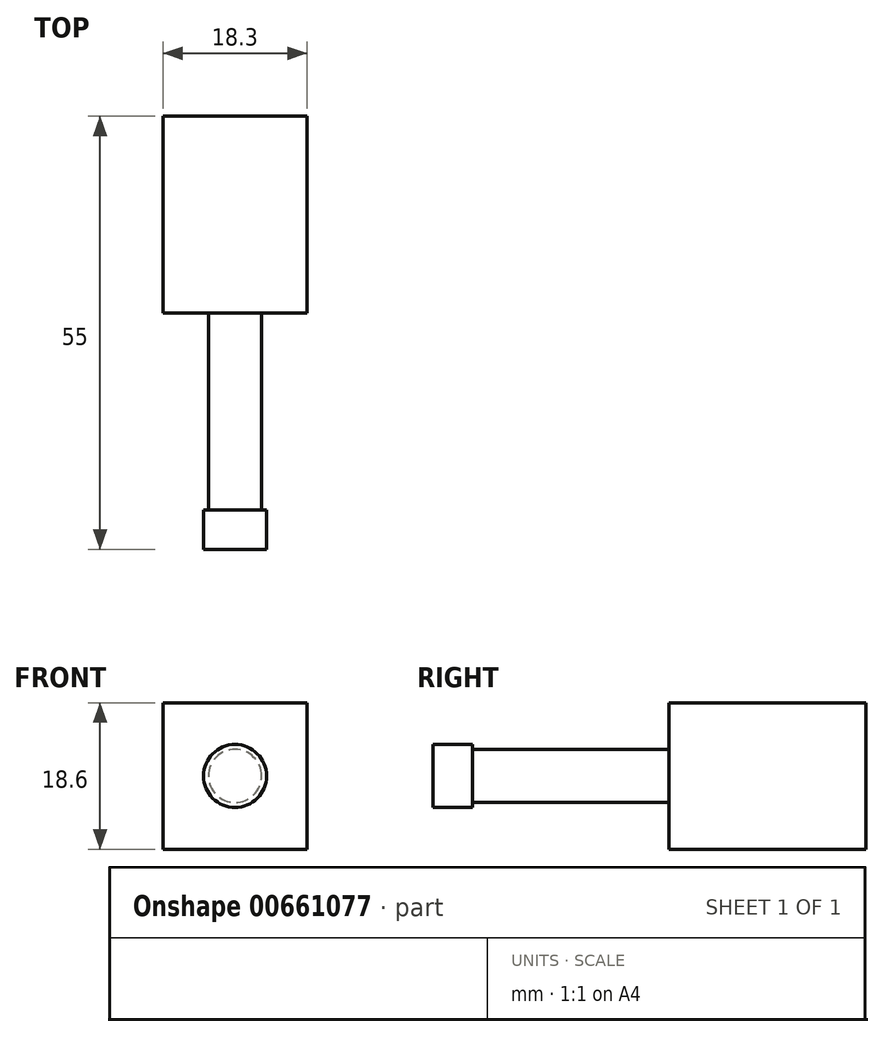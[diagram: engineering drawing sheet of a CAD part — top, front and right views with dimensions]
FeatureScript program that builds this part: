
annotation { "Feature Type Name" : "Feature", "Feature Type Description" : "" }
export const myFeature = defineFeature(function(context is Context, id is Id, definition is map)
    precondition{}
    {
        {
            var Q0;
            Q0=qCreatedBy(makeId("Front.planeOp"),FACE);
            var sketch = newSketch(context, id + "F0", { "sketchPlane" : qUnion([Q0])});
            skCircle(sketch, "E0", {"center": v(0, 0) * mm, "radius": 4 * mm});
            skSolve(sketch);
        }
        {
            var Q0;
            Q0 = qSketchRegion(id + "F0", true);
            extrude(context, id + "F1", {"entities" : qUnion([Q0]), "depth" : 5 * mm, "offsetDistance" : 25 * mm});
        }
        {
            var Q0;
            Q0=qCreatedBy(makeId("Front.planeOp"),FACE);
            var sketch = newSketch(context, id + "F2", { "sketchPlane" : qUnion([Q0])});
            skCircle(sketch, "E1", {"center": v(0, 0) * mm, "radius": 3.37 * mm});
            skSolve(sketch);
        }
        {
            var Q0;
            Q0 = qSketchRegion(id + "F2", true);
            extrude(context, id + "F3", {"entities" : qUnion([Q0]), "operationType" : NewBodyOperationType.ADD, "oppositeDirection" : true, "depth" : 25 * mm, "offsetDistance" : 25 * mm});
        }
        {
            var Q0;
            Q0=makeQuery(id+"F3.opExtrude","CAP_FACE",FACE,{"disambiguationData":[OSD([sQuery(id+"F2.wireOp",EDGE,"E1")])],"isStart":false});
            var sketch = newSketch(context, id + "F4", { "sketchPlane" : qUnion([Q0])});
            skLineSegment(sketch, "E2.bottom", {"start": v(9.15, -9.3) * mm, "end": v(-9.15, -9.3) * mm});
            skLineSegment(sketch, "E2.top", {"start": v(9.15, 9.3) * mm, "end": v(-9.15, 9.3) * mm});
            skLineSegment(sketch, "E2.left", {"start": v(9.15, -9.3) * mm, "end": v(9.15, 9.3) * mm});
            skLineSegment(sketch, "E2.right", {"start": v(-9.15, -9.3) * mm, "end": v(-9.15, 9.3) * mm});
            skPoint(sketch, "E2.middle", {"position": v(0, 0) * mm});
            skSolve(sketch);
        }
        {
            var Q0;
            Q0 = qSketchRegion(id + "F4", true);
            extrude(context, id + "F5", {"entities" : qUnion([Q0]), "operationType" : NewBodyOperationType.ADD, "depth" : 25 * mm, "offsetDistance" : 25 * mm});
        }
    });
